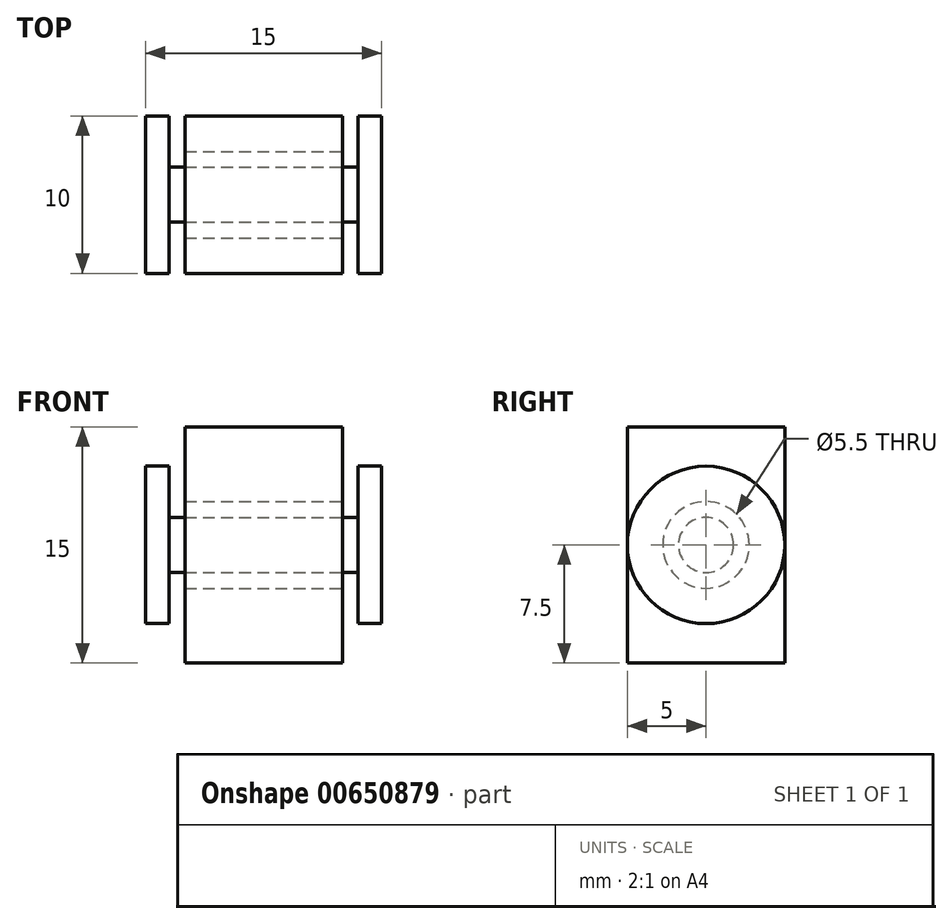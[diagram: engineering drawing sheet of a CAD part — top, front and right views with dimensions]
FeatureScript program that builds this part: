
annotation { "Feature Type Name" : "Feature", "Feature Type Description" : "" }
export const myFeature = defineFeature(function(context is Context, id is Id, definition is map)
    precondition{}
    {
        {
            var Q0;
            Q0=qCreatedBy(makeId("Top.planeOp"),FACE);
            var sketch = newSketch(context, id + "F0", { "sketchPlane" : qUnion([Q0])});
            skLineSegment(sketch, "E0.bottom", {"start": v(-5, 5) * mm, "end": v(5, 5) * mm});
            skLineSegment(sketch, "E0.top", {"start": v(-5, -5) * mm, "end": v(5, -5) * mm});
            skLineSegment(sketch, "E0.left", {"start": v(-5, 5) * mm, "end": v(-5, -5) * mm});
            skLineSegment(sketch, "E0.right", {"start": v(5, 5) * mm, "end": v(5, -5) * mm});
            skPoint(sketch, "E0.middle", {"position": v(0, 0) * mm});
            skSolve(sketch);
        }
        {
            var Q0;
            Q0=makeQuery(id+"F0.imprint","IMPRINT",FACE,{"disambiguationData":[TD([[makeQuery(id+"F0.imprint","IMPRINT",EDGE,{"derivedFrom":sQuery(id+"F0.wireOp",EDGE,"E0.bottom")}),-1.0]])]});
            extrude(context, id + "F1", {"entities" : qUnion([Q0]), "depth" : 15 * mm, "offsetDistance" : 25 * mm});
        }
        {
            var Q0;
            Q0=qCreatedBy(makeId("Right.planeOp"),FACE);
            cPlane(context, id + "F2", {"entities" : qUnion([Q0]), "cplaneType" : CPlaneType.OFFSET, "offset" : 0 * mm, "width" : 150 * mm, "height" : 150 * mm});
        }
        {
            var Q0;
            Q0=qCreatedBy(id+"F2.planeOp",FACE);
            var sketch = newSketch(context, id + "F3", { "sketchPlane" : qUnion([Q0])});
            skCircle(sketch, "E1", {"center": v(0, 7.5) * mm, "radius": 2.75 * mm});
            skSolve(sketch);
        }
        {
            var Q0;
            Q0 = qSketchRegion(id + "F3", true);
            extrude(context, id + "F4", {"entities" : qUnion([Q0]), "operationType" : NewBodyOperationType.REMOVE, "endBound" : BoundingType.SYMMETRIC, "oppositeDirection" : true, "depth" : 25 * mm, "offsetDistance" : 25 * mm});
        }
        {
            var Q0;
            Q0=qCreatedBy(makeId("Right.planeOp"),FACE);
            var sketch = newSketch(context, id + "F5", { "sketchPlane" : qUnion([Q0])});
            skCircle(sketch, "E2", {"center": v(0, 7.5) * mm, "radius": 1.75 * mm});
            skSolve(sketch);
        }
        {
            var Q0;
            Q0 = qSketchRegion(id + "F5", true);
            extrude(context, id + "F6", {"entities" : qUnion([Q0]), "operationType" : NewBodyOperationType.ADD, "endBound" : BoundingType.SYMMETRIC, "depth" : 12 * mm, "offsetDistance" : 25 * mm});
        }
        {
            var Q0;
            Q0=makeQuery(id+"F6.opExtrude","CAP_FACE",FACE,{"disambiguationData":[OSD([sQuery(id+"F5.wireOp",EDGE,"E2")])],"isStart":true});
            var sketch = newSketch(context, id + "F7", { "sketchPlane" : qUnion([Q0])});
            skCircle(sketch, "E3", {"center": v(0, 7.5) * mm, "radius": 5 * mm});
            skSolve(sketch);
        }
        {
            var Q0;
            Q0=makeQuery(id+"F7.imprint","IMPRINT",FACE,{"disambiguationData":[TD([[makeQuery(id+"F7.imprint","IMPRINT",EDGE,{"derivedFrom":sQuery(id+"F7.wireOp",EDGE,"E3")}),1.0]])]});
            var Q1;
            Q1=makeQuery(id+"F7.imprint","IMPRINT",FACE,{"disambiguationData":[TD([[makeQuery(id+"F7.imprint","IMPRINT",EDGE,{"derivedFrom":makeQuery(id+"F6.opExtrude","CAP_EDGE",EDGE,{"disambiguationData":[OSD([sQuery(id+"F5.wireOp",EDGE,"E2")])],"isStart":true})}),-1.0]])]});
            extrude(context, id + "F8", {"entities" : qUnion([Q0, Q1]), "operationType" : NewBodyOperationType.ADD, "depth" : 1.5 * mm, "offsetDistance" : 25 * mm});
        }
        {
            var Q0;
            Q0=makeQuery(id+"F6.opExtrude","SWEPT_BODY",BODY,{"disambiguationData":[OSD([sQuery(id+"F5.wireOp",EDGE,"E2")])]});
            var Q1;
            Q1=qCreatedBy(id+"F2.planeOp",FACE);
            mirror(context, id + "F9", {"operationType" : NewBodyOperationType.ADD, "entities" : qUnion([Q0]), "mirrorPlane" : qUnion([Q1])});
        }
    });
